# Revit family: NAU_Naughtone_Stng_Pullman_ChairPod
name_source: partatom
category: Furniture
revit_build: Autodesk Revit 2018 (Build: 20170223_1515(x64)
units: mm (PartAtom-declared; Revit-internal decimal feet)

## family parameters
Always vertical = Yes
Cut with Voids When Loaded = No
OmniClass Number = 23.40.20.00
OmniClass Title = General Furniture and Specialties
Room Calculation Point = No
Shared = Yes
Work Plane-Based = No

## types (8) — shared parameters
Assembly Code = E2020200
AssetType = Movable
BIMObjectName = NAU_Naughtone_Seating_Pullman_ChairPod
Category = Pr_40_50_12 : Chairs, seats and benches
DurationUnit = year
ExpectedLife = 10
Finish = Fabric upholstery
IfcExportAs = IfcFurnishingElementType
IfcExportType = CHAIR
Keynote = Pr_40_50_12
ManufacturerAddress = Knaresborough Tech Park, Manse Lane, Knaresborough, HG5 8LF
ManufacturerName = Naughtone
ManufacturerURL = www.naughtone.com
Material = Fabric, plywood frame, foam
NBSDescription = Seating
NBSReference = 45-35-72/352
Name = Seating_Pullman_ChairPod_Naughtone
NominalHeight = 1300 mm  [stored 4.26509 ft]
NominalLength = 1300 mm  [stored 4.26509 ft]
NominalWidth = 900 mm  [stored 2.95276 ft]
NumberOfChairs = 1
ProductInformation = www.naughtone.com/products/pullmanchair/
Shape = Rectangular
Size = 1300 x 900 x 1300 mm
URL = www.naughtone.com
Uniclass2015Code = Pr_40_50_12
Uniclass2015Title = Chairs, seats and benches
Uniclass2015Version = Products v1.22
Version = 1
WarrantyDescription = Request warranty information from naughtone
WarrantyDurationLabor = 10
WarrantyDurationParts = 10
WarrantyDurationUnit = year
zero-valued in all types: WorksurfaceArea

## per-type parameters (varying)
| type | Features | HasLegsLeft | HasLegsRight | HasScreenLeft | HasScreenRight | Is4Legs | IsLeftPlinth | IsLeftTablet | IsPlinth | IsRightPlinth | IsRightTablet | Model | ModelNumber |
| Pullman Chair Pod - Screen Left on Plinth | Available in two version of tone fabric. | No | No | Yes | No | No | Yes | No | Yes | No | No | PULPHLAP | PULPHLAP |
| Pullman Chair Pod - Screen Right on Plinth | Available in two version of tone fabric. | No | No | No | Yes | No | No | No | Yes | Yes | No | PULPHRAP | PULPHRAP |
| Pullman Chair Pod - Screen Left on Legs | Available in two version of tone fabric | Yes | No | Yes | No | Yes | No | No | No | No | No | PULPHLA* | PULPHLA* |
| Pullman Chair Pod - Screen Right on Legs | Available in two version of tone fabric. | No | Yes | No | Yes | Yes | No | No | No | No | No | PULPHRA* | PULPHRA* |
| Pullman Chair Pod - Screen Left on Plinth with Tablet Arm | Available in two version of tone fabric. | No | No | Yes | No | No | Yes | Yes | Yes | No | No | PULPHLAPT | PULPHLAPT |
| Pullman Chair Pod - Screen Right on Plinth with Tablet Arm | Available in two version of tone fabric. | No | No | No | Yes | No | No | No | Yes | Yes | Yes | PULPHRAPT | PULPHRAPT |
| Pullman Chair Pod - Screen Left on Legs with Tablet Arm | Available in two version of tone fabric. | Yes | No | Yes | No | Yes | No | Yes | No | No | No | PULPHLA*T | PULPHLA*T |
| Pullman Chair Pod - Screen Right on Legs with Tablet Arm | Available in two version of tone fabric. | No | Yes | No | Yes | Yes | No | No | No | No | Yes | PULPHRA*T | PULPHRA*T |

note: column(s) folded — value = type name in every type: Description, ModelReference

note: [stored X ft] marks values corroborated as IEEE doubles in the binary element streams (Revit-internal decimal feet)

## geometry (parser evidence)
native form markers: Sweep x5
no freeform markers — native parametric forms only
